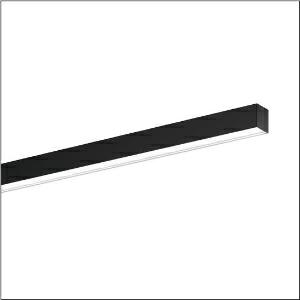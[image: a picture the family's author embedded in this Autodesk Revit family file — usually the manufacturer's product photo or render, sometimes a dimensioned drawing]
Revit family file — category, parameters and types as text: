
# Revit family: silica_r__21_51mx20tat2b_5805
name_source: partatom
category: Lighting Fixtures
units: mm (PartAtom-declared; Revit-internal decimal feet)

## family parameters
Cut with Voids When Loaded = No
Host = Face
Light Source = No
Part Type = Normal
Room Calculation Point = No
Round Connector Dimension = Use Diameter
Shared = No

## types (1)
- --- (1 x LED, 2400 lm, 20.5 W, 6500K)
    Apparent Load = 21 VA
    CIE Flux Codes = 48 79 96 100 100
    Color Rendering = 80
    Color Temperature = 6500K
    Default Elevation = 1800 mm
    Description = Silica® 21, office luminaire, primary optical cover: cover, of PMMA, opal, light emission: direct distribution, primary light characteristic: symmetric, installation type: surface-mounted, LED, rated luminous flux: 2.400lm, luminous efficacy: 112lm/W, light colour: 8tw, colour temperature: 2700..6500K, control gear: ECG DALI, with terminal, 3+2-pole, max. 2.5mm², mains connection: 220..240V, AC, 50/60Hz, rated input power: 21.5W, luminaire housing, of aluminium, jet black (RAL 9005), length: 1.204mm, width: 53mm, height: 53mm, protection rating (complete): IP20, insulation class (complete): insulation class I (protective earthing), certification: CE, permissible operating ambient temperature: 0..+35°C, standard: EN 50419, packaging unit: 1 piece
    Height = 0 mm  [stored 0 ft]
    Lamp = 1 x LED
    Lamp Light Flux = 2400 lm
    Lamp Power = 20.5 W
    Lamp count = 1
    Length = 1204 mm
    Luminous efficacy = 117 lm/W
    Manufacturer = Siteco
    ModVariant = No
    Model = 51MX20TAT2B
    Mounting Place = Ceiling
    Mounting Type = Recessed
    Number of Poles = 1
    OnlyDefault = Yes
    Power Factor = 1
    Product Name = Silica® 21
    Product group = office luminaire | ceiling recessed
    ProductGroupID = 401
    Protection Class = Protection class I
    Protection Degree = IP 20
    RLX_Detail_Level = 1
    RLX_Emergency_Light_Flux = 0 lm
    RLX_Emergency_Type = 0
    RLX_Emergency_Type_DB = No
    RlxData = <blob elided: 25757 chars, md5=c99e53b1>
    Socket = socket
    Standby Power = 0 W
    System Light Flux = 2400 lm
    System Power = 21 W
    Type Comments = individual setting
    Type Image = l_1297760.jpg
    URL = http://relux.com
    VarID = @adj_071017
    Voltage = 0 V
    Weight = 0.00 kg
    Width = 53 mm

note: [stored X ft] marks values corroborated as IEEE doubles in the binary element streams (Revit-internal decimal feet)

## geometry (parser evidence)
native form markers: Blend x4, Sweep x9
no freeform markers — native parametric forms only
